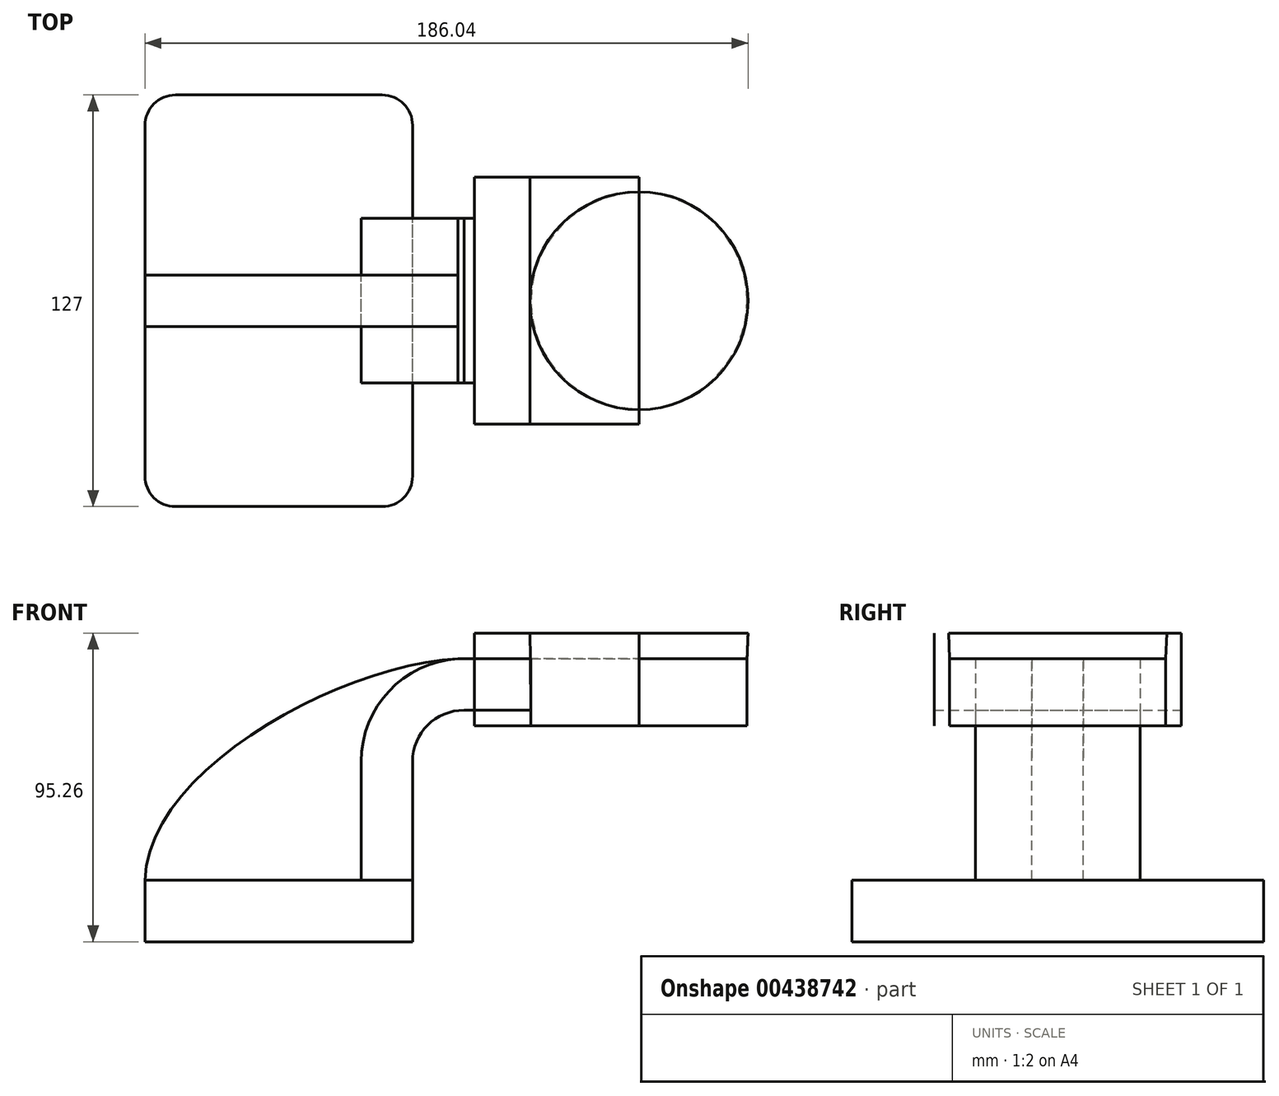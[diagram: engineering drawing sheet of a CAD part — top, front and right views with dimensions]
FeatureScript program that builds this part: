
annotation { "Feature Type Name" : "Feature", "Feature Type Description" : "" }
export const myFeature = defineFeature(function(context is Context, id is Id, definition is map)
    precondition{}
    {
        {
            var Q0;
            Q0=qCreatedBy(makeId("Front.planeOp"),FACE);
            var sketch = newSketch(context, id + "F0", { "sketchPlane" : qUnion([Q0])});
            skLineSegment(sketch, "E0.bottom", {"start": v(-41.28, 9.52) * mm, "end": v(41.28, 9.53) * mm});
            skLineSegment(sketch, "E0.top", {"start": v(-41.28, -9.52) * mm, "end": v(41.28, -9.52) * mm});
            skLineSegment(sketch, "E0.left", {"start": v(-41.28, 9.52) * mm, "end": v(-41.27, -9.53) * mm});
            skLineSegment(sketch, "E0.right", {"start": v(41.28, 9.53) * mm, "end": v(41.28, -9.52) * mm});
            skPoint(sketch, "E0.middle", {"position": v(0, 0) * mm});
            skLineSegment(sketch, "E1.bottom", {"start": v(60.33, 85.73) * mm, "end": v(111.13, 85.73) * mm});
            skLineSegment(sketch, "E1.top", {"start": v(60.33, 57.15) * mm, "end": v(111.13, 57.15) * mm});
            skLineSegment(sketch, "E1.left", {"start": v(60.33, 85.73) * mm, "end": v(60.33, 57.15) * mm});
            skLineSegment(sketch, "E1.right", {"start": v(111.13, 85.73) * mm, "end": v(111.13, 57.15) * mm});
            skPoint(sketch, "E1.middle", {"position": v(85.73, 71.44) * mm});
            skLineSegment(sketch, "E2", {"start": v(41.27, 9.53) * mm, "end": v(41.27, 46.05) * mm});
            skArc(sketch, "E3", {"start": v(41.27, 46.05) * mm, "mid": v(45.92, 57.28) * mm, "end": v(57.15, 61.93) * mm});
            skLineSegment(sketch, "E4", {"start": v(57.15, 61.93) * mm, "end": v(77.8, 61.93) * mm});
            skLineSegment(sketch, "E5.0", {"start": v(57.15, 77.8) * mm, "end": v(77.8, 77.8) * mm});
            skArc(sketch, "E5.1", {"start": v(25.4, 46.05) * mm, "mid": v(34.7, 68.5) * mm, "end": v(57.15, 77.8) * mm});
            skLineSegment(sketch, "E5.2", {"start": v(25.4, 9.53) * mm, "end": v(25.4, 46.05) * mm});
            skLineSegment(sketch, "E6", {"start": v(77.8, 77.8) * mm, "end": v(77.8, 61.93) * mm});
            skFitSpline(sketch, "E7", {"points": [v(-41.28, 9.53) * mm, v(57.15, 77.8) * mm], "startDerivative": vector(2.56, 104.44) * mm, "endDerivative": vector(106.93, 1.54) * mm});
            skLineSegment(sketch, "E8", {"start": v(77.8, 61.93) * mm, "end": v(77.8, 57.15) * mm});
            skLineSegment(sketch, "E9", {"start": v(77.8, 57.15) * mm, "end": v(77.8, 77.8) * mm});
            skLineSegment(sketch, "E10", {"start": v(77.49, 85.73) * mm, "end": v(77.8, 77.8) * mm});
            skLineSegment(sketch, "E11", {"start": v(77.49, 85.73) * mm, "end": v(77.8, 57.15) * mm});
            skSolve(sketch);
        }
        {
            var Q0;
            Q0=makeQuery(id+"F0.imprint","IMPRINT",FACE,{"disambiguationData":[TD([[makeQuery(id+"F0.imprint","IMPRINT",EDGE,{"derivedFrom":sQuery(id+"F0.wireOp",EDGE,"E0.top")}),1.0]])]});
            extrude(context, id + "F1", {"entities" : qUnion([Q0]), "endBound" : BoundingType.SYMMETRIC, "depth" : 127 * mm});
        }
        {
            var Q0;
            {var subQ1=sQuery(id+"F0.wireOp",EDGE,"E2");Q0=makeQuery(id+"F0.imprint","IMPRINT",FACE,{"disambiguationData":[TD([[makeQuery(id+"F0.imprint","IMPRINT",EDGE,{"derivedFrom":subQ1}),1.0]])]});}
            extrude(context, id + "F2", {"entities" : qUnion([Q0]), "endBound" : BoundingType.SYMMETRIC, "depth" : 50.8 * mm});
        }
        {
            var Q0;
            {var subQ4=sQuery(id+"F0.wireOp",EDGE,"E1.right");Q0=makeQuery(id+"F0.imprint","IMPRINT",FACE,{"disambiguationData":[TD([[makeQuery(id+"F0.imprint","IMPRINT",EDGE,{"derivedFrom":subQ4}),-1.0]])]});}
            var Q1;
            {var subQ0=sQuery(id+"F0.wireOp",EDGE,"E5.0");var subQ1=sQuery(id+"F0.wireOp",EDGE,"E1.left");var subQ2=makeQuery(id+"F0.imprint","INTERSECT",VERTEX,{"derivedFrom":[subQ1,subQ0]});Q1=makeQuery(id+"F0.imprint","IMPRINT",FACE,{"disambiguationData":[TD([[makeQuery(id+"F0.imprint","IMPRINT",EDGE,{"disambiguationData":[TD([[subQ2,-1.0]])],"derivedFrom":subQ1}),1.0]])]});}
            var Q2;
            {var subQ3=sQuery(id+"F0.wireOp",EDGE,"E10");Q2=makeQuery(id+"F0.imprint","IMPRINT",FACE,{"disambiguationData":[TD([[makeQuery(id+"F0.imprint","IMPRINT",EDGE,{"derivedFrom":subQ3}),-1.0]])]});}
            extrude(context, id + "F3", {"entities" : qUnion([Q0, Q1, Q2]), "endBound" : BoundingType.SYMMETRIC, "depth" : 76.2 * mm});
        }
        {
            var Q0;
            {var subQ0=sQuery(id+"F0.wireOp",EDGE,"E1.left");var subQ1=sQuery(id+"F0.wireOp",EDGE,"E1.top");var subQ2=makeQuery(id+"F0.imprint","INTERSECT",VERTEX,{"derivedFrom":[subQ1,subQ0]});Q0=makeQuery(id+"F0.imprint","IMPRINT",FACE,{"disambiguationData":[TD([[makeQuery(id+"F0.imprint","IMPRINT",EDGE,{"disambiguationData":[TD([[subQ2,-1.0]])],"derivedFrom":subQ1}),1.0]])]});}
            extrude(context, id + "F4", {"entities" : qUnion([Q0]), "endBound" : BoundingType.SYMMETRIC, "depth" : 76.2 * mm});
        }
        {
            var Q0;
            {var subQ0=sQuery(id+"F0.wireOp",EDGE,"E1.right");Q0=makeQuery(id+"F0.imprint","IMPRINT",FACE,{"disambiguationData":[TD([[makeQuery(id+"F0.imprint","IMPRINT",EDGE,{"derivedFrom":subQ0}),-1.0]])]});}
            var Q1;
            Q1=sQuery(id+"F0.wireOp",EDGE,"E1.right");
            revolve(context, id + "F5", {"entities" : qUnion([Q0]), "axis" : qUnion([Q1]), "revolveType" : RevolveType.FULL});
        }
        {
            var Q0;
            {var subQ3=sQuery(id+"F0.wireOp",EDGE,"E5.2");Q0=makeQuery(id+"F0.imprint","IMPRINT",FACE,{"disambiguationData":[TD([[makeQuery(id+"F0.imprint","IMPRINT",EDGE,{"derivedFrom":subQ3}),1.0]])]});}
            extrude(context, id + "F6", {"entities" : qUnion([Q0]), "endBound" : BoundingType.SYMMETRIC, "depth" : 15.88 * mm});
        }
        {
            var Q0;
            {var subQ0=sQuery(id+"F0.wireOp",EDGE,"E1.left");var subQ1=sQuery(id+"F0.wireOp",EDGE,"E1.bottom");var subQ2=makeQuery(id+"F0.imprint","INTERSECT",VERTEX,{"derivedFrom":[subQ1,subQ0]});Q0=makeQuery(id+"F0.imprint","IMPRINT",FACE,{"disambiguationData":[TD([[makeQuery(id+"F0.imprint","IMPRINT",EDGE,{"disambiguationData":[TD([[subQ2,-1.0]])],"derivedFrom":subQ0}),1.0]])]});}
            extrude(context, id + "F7", {"entities" : qUnion([Q0]), "endBound" : BoundingType.SYMMETRIC, "depth" : 76.2 * mm});
        }
        {
            var Q0;
            Q0=makeQuery(id+"F1.opExtrude","CAP_EDGE",EDGE,{"disambiguationData":[OSD([sQuery(id+"F0.wireOp",EDGE,"E0.left")])],"isStart":false});
            var Q1;
            Q1=makeQuery(id+"F1.opExtrude","CAP_EDGE",EDGE,{"disambiguationData":[OSD([sQuery(id+"F0.wireOp",EDGE,"E0.right")])],"isStart":false});
            var Q2;
            Q2=makeQuery(id+"F1.opExtrude","CAP_EDGE",EDGE,{"disambiguationData":[OSD([sQuery(id+"F0.wireOp",EDGE,"E0.left")])],"isStart":true});
            var Q3;
            Q3=makeQuery(id+"F1.opExtrude","CAP_EDGE",EDGE,{"disambiguationData":[OSD([sQuery(id+"F0.wireOp",EDGE,"E0.right")])],"isStart":true});
            fillet(context, id + "F8", {"entities" : qUnion([Q0, Q1, Q2, Q3]), "radius" : 9.4 * mm, "tangentPropagation" : true, "allowEdgeOverflow" : false});
        }
    });
